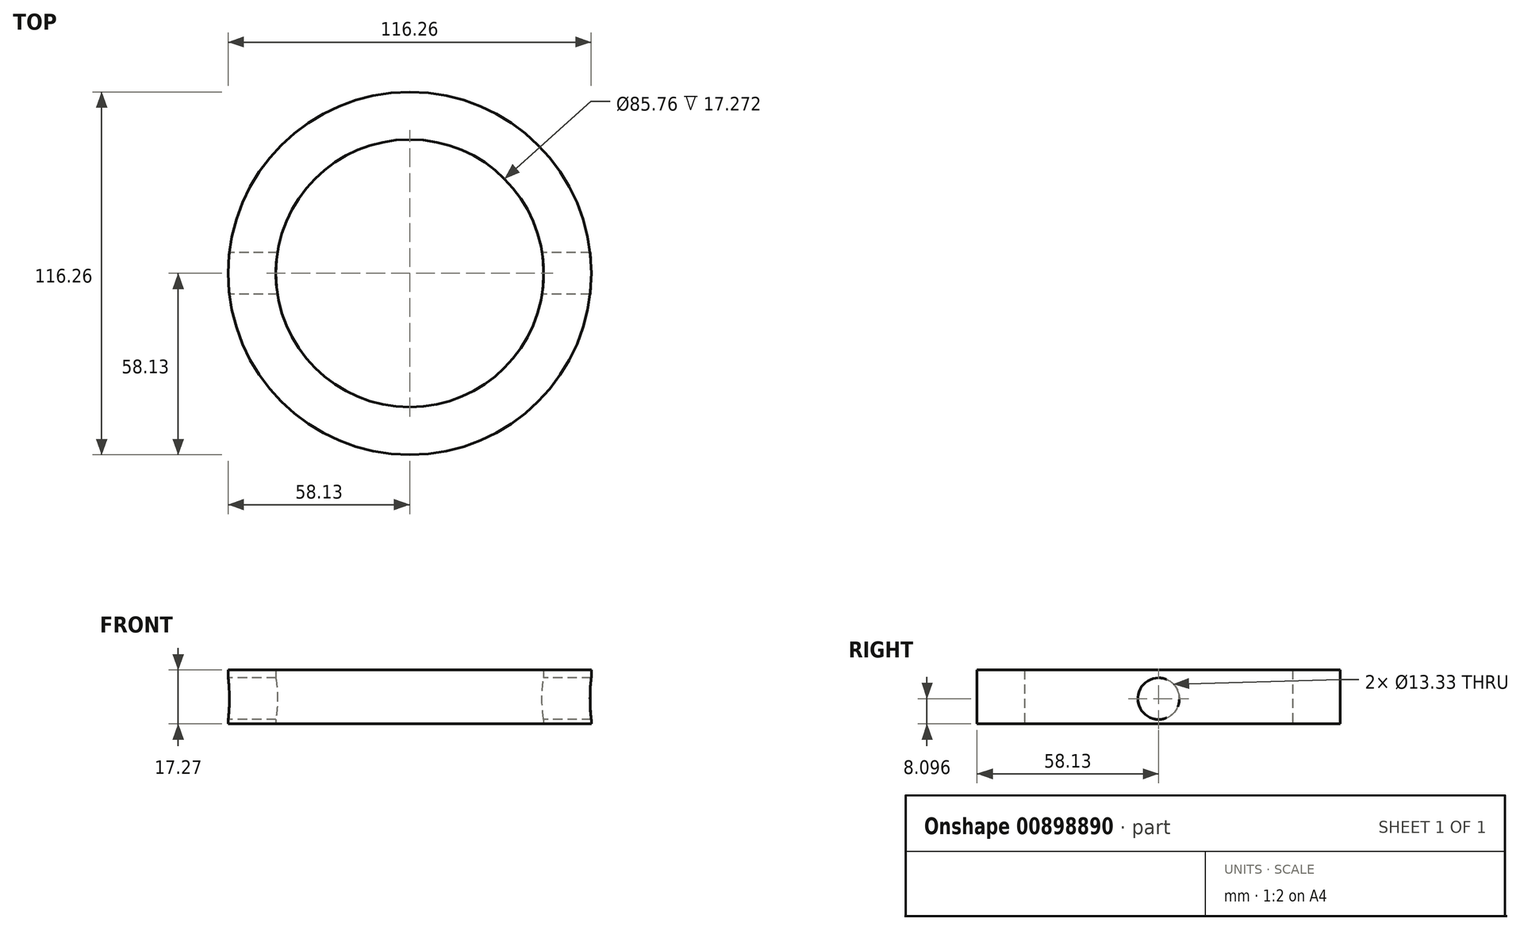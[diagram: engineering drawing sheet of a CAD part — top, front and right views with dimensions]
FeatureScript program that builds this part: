
annotation { "Feature Type Name" : "Feature", "Feature Type Description" : "" }
export const myFeature = defineFeature(function(context is Context, id is Id, definition is map)
    precondition{}
    {
        {
            var Q0;
            Q0=qCreatedBy(makeId("Top.planeOp"),FACE);
            var sketch = newSketch(context, id + "F0", { "sketchPlane" : qUnion([Q0])});
            skCircle(sketch, "E0", {"center": v(0, 0) * mm, "radius": 58.13 * mm});
            skCircle(sketch, "E1", {"center": v(0, 0) * mm, "radius": 42.88 * mm});
            skSolve(sketch);
        }
        {
            var Q0;
            Q0=makeQuery(id+"F0.imprint","IMPRINT",FACE,{"disambiguationData":[TD([[makeQuery(id+"F0.imprint","IMPRINT",EDGE,{"derivedFrom":sQuery(id+"F0.wireOp",EDGE,"E0")}),1.0]])]});
            extrude(context, id + "F1", {"entities" : qUnion([Q0]), "depth" : 17.27 * mm, "offsetDistance" : 25.4 * mm});
        }
        {
            var Q0;
            Q0=qCreatedBy(makeId("Right.planeOp"),FACE);
            var sketch = newSketch(context, id + "F2", { "sketchPlane" : qUnion([Q0])});
            skCircle(sketch, "E2", {"center": v(0, 8.34) * mm, "radius": 6.03 * mm});
            skSolve(sketch);
        }
        {
            var Q0;
            Q0=qSketchRegion(id+"F2",true);
            extrude(context, id + "F3", {"entities" : qUnion([Q0]), "operationType" : NewBodyOperationType.REMOVE, "depth" : 121.92 * mm, "offsetDistance" : 25.4 * mm});
        }
        {
            var Q0;
            Q0=qCreatedBy(makeId("Right.planeOp"),FACE);
            var sketch = newSketch(context, id + "F4", { "sketchPlane" : qUnion([Q0])});
            skCircle(sketch, "E3", {"center": v(0, 8.1) * mm, "radius": 6.67 * mm});
            skSolve(sketch);
        }
        {
            var Q0;
            Q0=qSketchRegion(id+"F4",true);
            extrude(context, id + "F5", {"entities" : qUnion([Q0]), "operationType" : NewBodyOperationType.REMOVE, "endBound" : BoundingType.SYMMETRIC, "depth" : 163.58 * mm, "offsetDistance" : 25.4 * mm});
        }
    });
